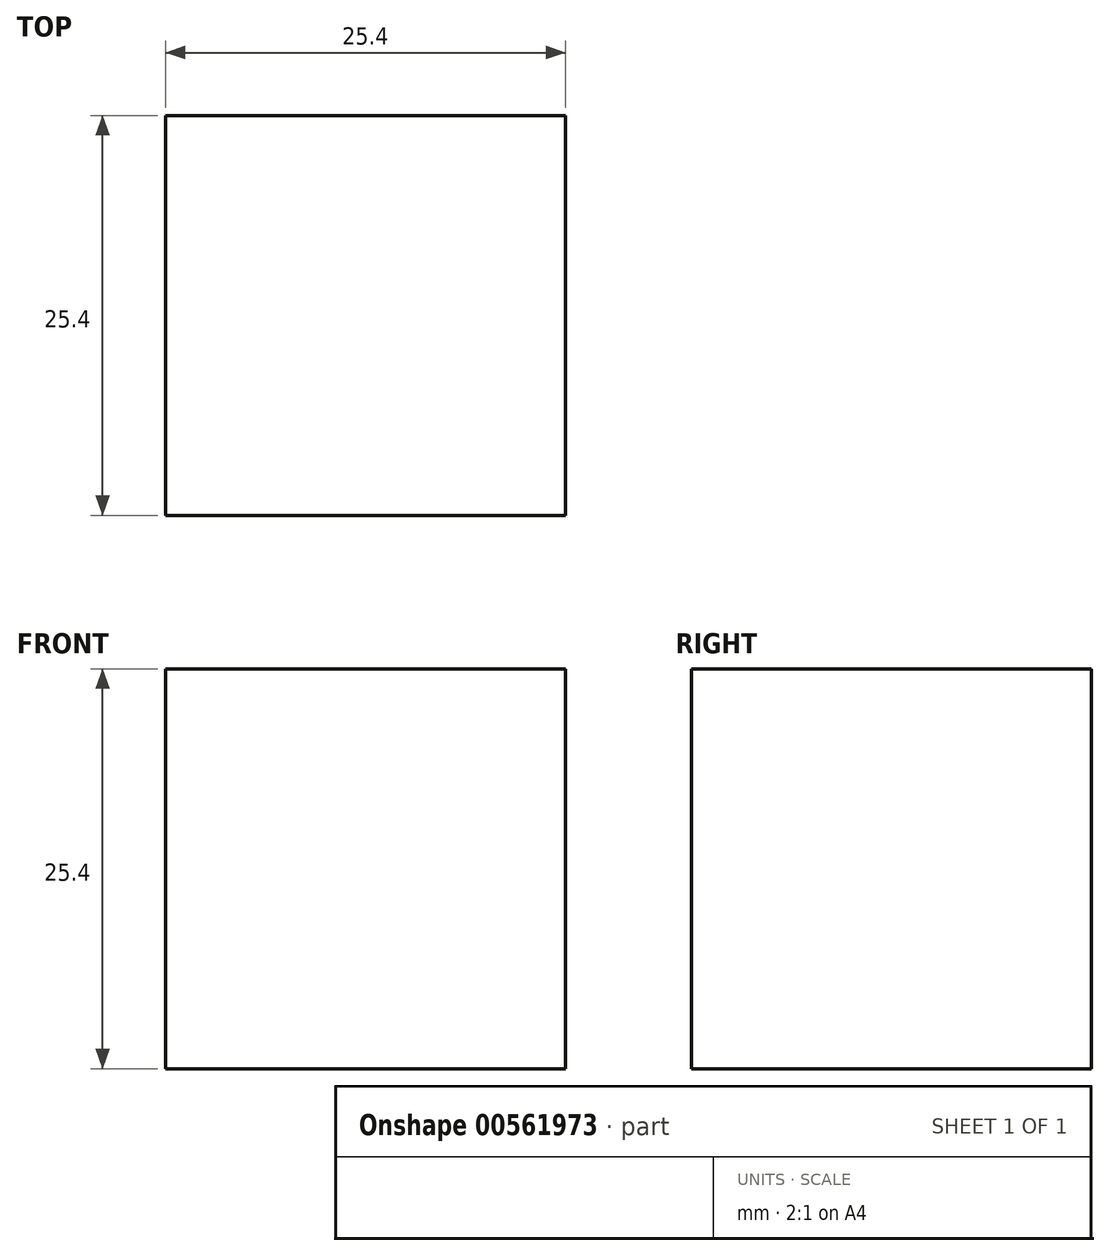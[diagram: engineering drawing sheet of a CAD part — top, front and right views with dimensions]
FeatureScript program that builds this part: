
annotation { "Feature Type Name" : "Feature", "Feature Type Description" : "" }
export const myFeature = defineFeature(function(context is Context, id is Id, definition is map)
    precondition{}
    {
        {
            var Q0;
            Q0=qCreatedBy(makeId("Front.planeOp"),FACE);
            var sketch = newSketch(context, id + "F0", { "sketchPlane" : qUnion([Q0])});
            skLineSegment(sketch, "E0.bottom", {"start": v(-42.18, 40.29) * mm, "end": v(-16.78, 40.29) * mm});
            skLineSegment(sketch, "E0.top", {"start": v(-42.18, 14.89) * mm, "end": v(-16.78, 14.89) * mm});
            skLineSegment(sketch, "E0.left", {"start": v(-42.18, 40.29) * mm, "end": v(-42.18, 14.89) * mm});
            skLineSegment(sketch, "E0.right", {"start": v(-16.78, 40.29) * mm, "end": v(-16.78, 14.89) * mm});
            skSolve(sketch);
        }
        {
            var Q0;
            Q0=makeQuery(id+"F0.imprint","IMPRINT",FACE,{"disambiguationData":[TD([[makeQuery(id+"F0.imprint","IMPRINT",EDGE,{"derivedFrom":sQuery(id+"F0.wireOp",EDGE,"E0.bottom")}),-1.0]])]});
            extrude(context, id + "F1", {"entities" : qUnion([Q0]), "depth" : 25.4 * mm, "offsetDistance" : 25.4 * mm});
        }
    });
